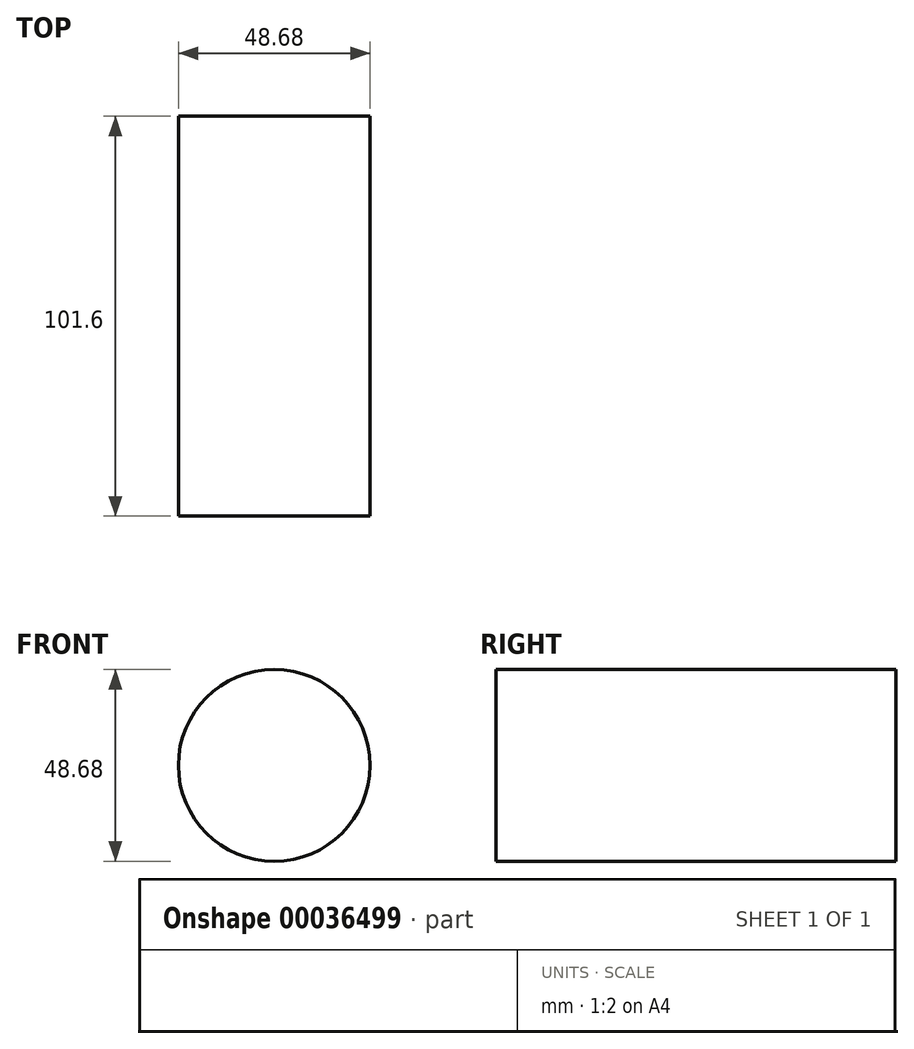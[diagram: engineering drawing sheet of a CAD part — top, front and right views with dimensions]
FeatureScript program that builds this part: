
annotation { "Feature Type Name" : "Feature", "Feature Type Description" : "" }
export const myFeature = defineFeature(function(context is Context, id is Id, definition is map)
    precondition{}
    {
        {
            var Q0;
            Q0=qCreatedBy(makeId("Front.planeOp"),FACE);
            var sketch = newSketch(context, id + "F0", { "sketchPlane" : qUnion([Q0])});
            skCircle(sketch, "E0", {"center": v(0, 0) * mm, "radius": 24.34 * mm});
            skSolve(sketch);
        }
        {
            var Q0;
            Q0=makeQuery(id+"F0.imprint","IMPRINT",FACE,{"disambiguationData":[TD([[makeQuery(id+"F0.imprint","IMPRINT",EDGE,{"derivedFrom":sQuery(id+"F0.wireOp",EDGE,"E0")}),1.0]])]});
            extrude(context, id + "F1", {"entities" : qUnion([Q0]), "depth" : 76.2 * mm, "hasSecondDirection" : true, "secondDirectionOppositeDirection" : true, "secondDirectionDepth" : 25.4 * mm});
        }
    });
